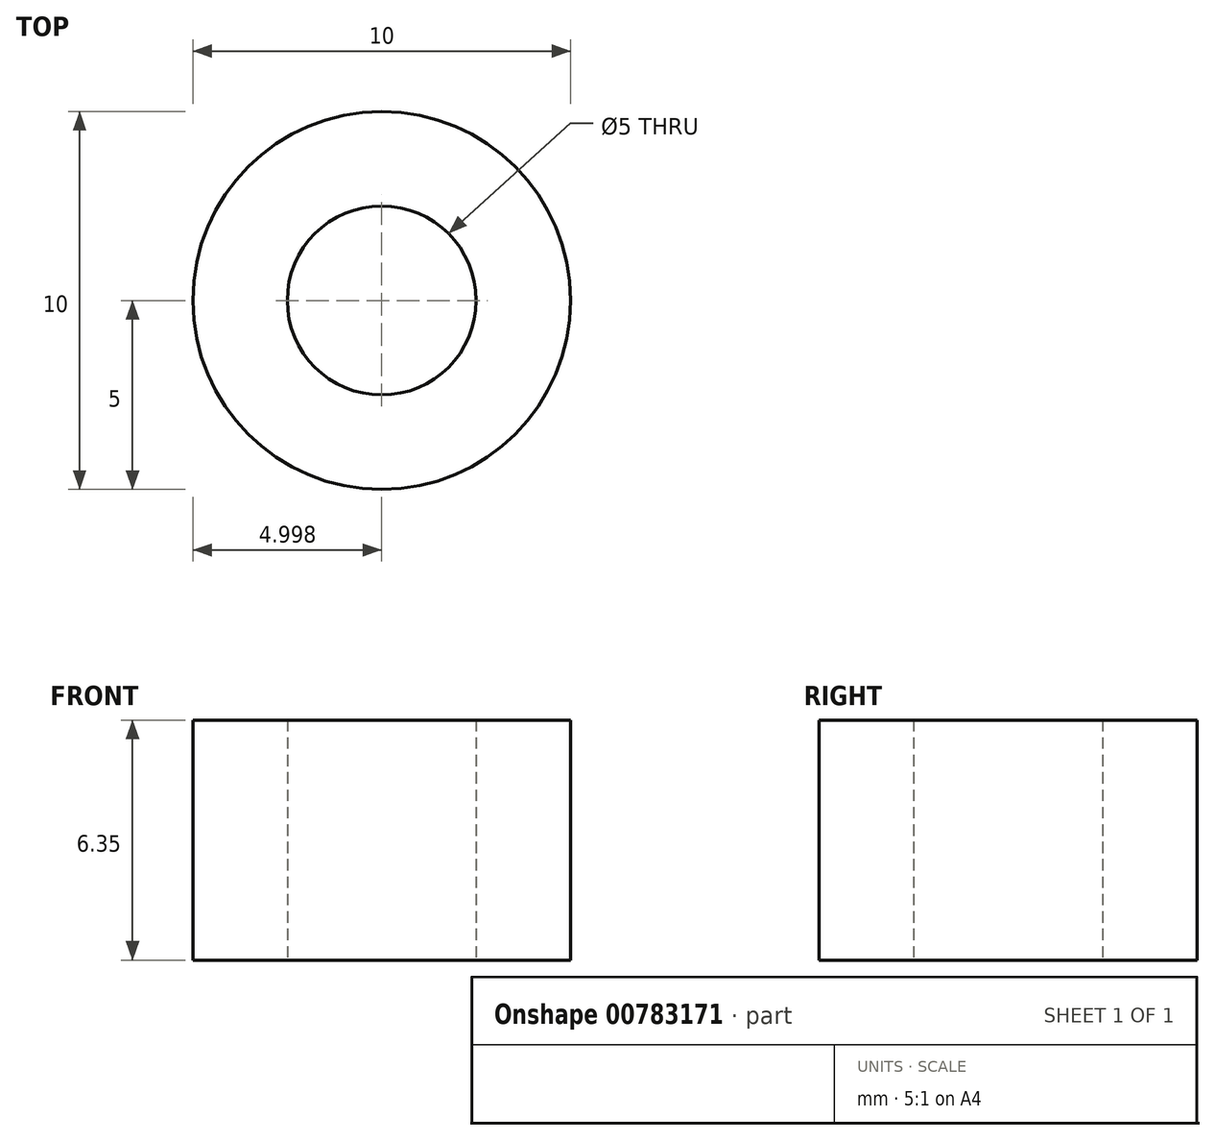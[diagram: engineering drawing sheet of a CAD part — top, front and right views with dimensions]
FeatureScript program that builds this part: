
annotation { "Feature Type Name" : "Feature", "Feature Type Description" : "" }
export const myFeature = defineFeature(function(context is Context, id is Id, definition is map)
    precondition{}
    {
        {
            var Q0;
            Q0=qCreatedBy(makeId("Top.planeOp"),FACE);
            var sketch = newSketch(context, id + "F0", { "sketchPlane" : qUnion([Q0])});
            skCircle(sketch, "E0", {"center": v(-23.42, -7.85) * mm, "radius": 5 * mm});
            skCircle(sketch, "E1", {"center": v(-23.42, -7.85) * mm, "radius": 2.5 * mm});
            skSolve(sketch);
        }
        {
            var Q0;
            Q0=qSketchRegion(id+"F0",true);
            extrude(context, id + "F1", {"entities" : qUnion([Q0]), "depth" : 6.35 * mm});
        }
    });
